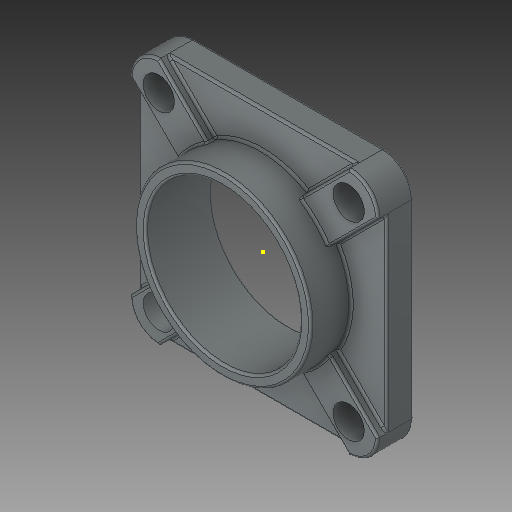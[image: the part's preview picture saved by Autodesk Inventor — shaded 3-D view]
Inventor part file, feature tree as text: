
AUTODESK INVENTOR PART (.ipt)
format: ipt  version: 2019 (Build 230136000, 136)  size: 446,976 bytes
history: native  units: mm
features: sketch x10, extrude x5, fillet x3, pattern_linear x1, pattern_circular x1
ambient origin geometry x8: Origin, YZ Plane, XZ Plane, XY Plane, X Axis, Y Axis, Z Axis, Center Point
bodies: Solid1 (feature_tree)
feature tree (20):
  extrude  "Extrusion1"  Depth=111.0mm
  sketch  "Sketch2"  dims[d4=13.0mm d5=14.0mm]
  fillet  "Fillet1"  Radius=12.0mm
  extrude  "Extrusion2"  Depth=14.0mm
  pattern_linear  "Rectangular Pattern1"  Count1=2 Spacing1=85.0mm
  extrude  "Extrusion3"  Depth=79.0mm
  extrude  "Extrusion4"  Depth=18.0mm TaperAngle=0.0deg
  sketch  "Sketch6"  dims[d18=80.0mm d19=0.0mm d21=135.0deg]
  extrude  "Extrusion5"  TaperAngle=135.0deg  [1 undecoded]
  pattern_circular  "Circular Pattern1"  Count=4 Angle=360.0deg
  fillet  "Fillet2"  Radius=1.0mm
  fillet  "Fillet3"  Radius=1.0mm
  sketch  "Sketch8"  dims[d23=4.0mm d24=0.0mm d25=40.0mm d26=360.0deg d28=1.0mm d29=1.0mm]
  sketch  "Sketch9"
  sketch  "Sketch10"
  sketch  "Sketch1"  dims[d0=111.0mm d1=111.0mm d2=12.0mm d3=0.0mm]
  sketch  "Sketch3"  dims[d6=12.0mm d7=0.0mm d8=20.0mm d10=85.0mm]
  sketch  "Sketch4"  dims[d11=20.0mm d13=85.0mm d14=79.0mm]
  sketch  "Sketch5"  dims[d15=69.0mm d16=18.0mm d17=0.0mm]
  sketch  "Sketch7"  dims[d22=135.0deg]
note: 1 required parameter value undecoded (feature->parameter linkage not recoverable at this tier; creation-order binding heuristic only, values carry confidence <= 0.55)
